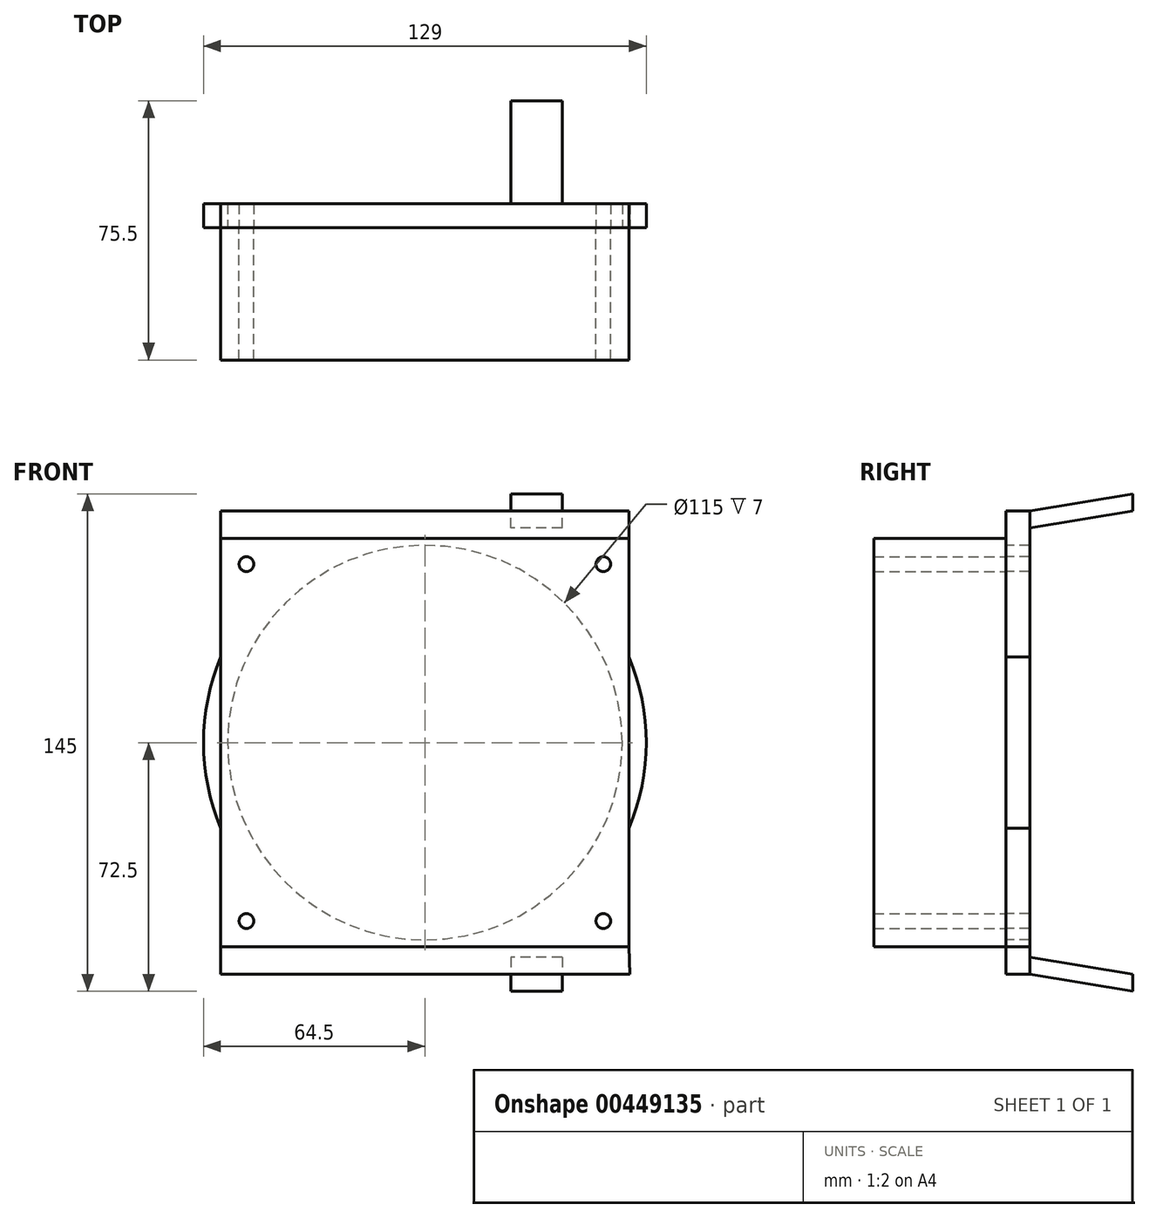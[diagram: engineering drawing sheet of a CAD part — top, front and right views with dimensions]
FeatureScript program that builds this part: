
annotation { "Feature Type Name" : "Feature", "Feature Type Description" : "" }
export const myFeature = defineFeature(function(context is Context, id is Id, definition is map)
    precondition{}
    {
        {
            var Q0;
            Q0=qCreatedBy(makeId("Front.planeOp"),FACE);
            var sketch = newSketch(context, id + "F0", { "sketchPlane" : qUnion([Q0])});
            skLineSegment(sketch, "E0.bottom", {"start": v(-48.5, 67.5) * mm, "end": v(48.5, 67.5) * mm});
            skLineSegment(sketch, "E0.top", {"start": v(-48.5, -67.5) * mm, "end": v(48.5, -67.5) * mm});
            skLineSegment(sketch, "E0.left", {"start": v(-48.5, 67.5) * mm, "end": v(-48.5, -67.5) * mm});
            skLineSegment(sketch, "E0.right", {"start": v(48.5, 67.5) * mm, "end": v(48.5, -67.5) * mm});
            skPoint(sketch, "E0.middle", {"position": v(0, 0) * mm});
            skSolve(sketch);
        }
        {
            var Q0;
            Q0=qCreatedBy(makeId("Front.planeOp"),FACE);
            var sketch = newSketch(context, id + "F1", { "sketchPlane" : qUnion([Q0])});
            skLineSegment(sketch, "E1.bottom", {"start": v(52, 52) * mm, "end": v(-52, 52) * mm, "construction": true});
            skLineSegment(sketch, "E1.top", {"start": v(52, -52) * mm, "end": v(-52, -52) * mm, "construction": true});
            skLineSegment(sketch, "E1.left", {"start": v(52, 52) * mm, "end": v(52, -52) * mm, "construction": true});
            skLineSegment(sketch, "E1.right", {"start": v(-52, 52) * mm, "end": v(-52, -52) * mm, "construction": true});
            skPoint(sketch, "E1.middle", {"position": v(0, 0) * mm});
            skLineSegment(sketch, "E2.bottom", {"start": v(-59.5, -59.5) * mm, "end": v(59.5, -59.5) * mm});
            skLineSegment(sketch, "E2.top", {"start": v(-59.5, 59.5) * mm, "end": v(59.5, 59.5) * mm});
            skLineSegment(sketch, "E2.left", {"start": v(-59.5, -59.5) * mm, "end": v(-59.5, 59.5) * mm});
            skLineSegment(sketch, "E2.right", {"start": v(59.5, -59.5) * mm, "end": v(59.5, 59.5) * mm});
            skCircle(sketch, "E3", {"center": v(-52, 52) * mm, "radius": 2.15 * mm});
            skCircle(sketch, "E4.MirrorC", {"center": v(52, 52) * mm, "radius": 2.15 * mm});
            skCircle(sketch, "E5.MirrorC", {"center": v(-52, -52) * mm, "radius": 2.15 * mm});
            skCircle(sketch, "E6.MirrorC", {"center": v(52, -52) * mm, "radius": 2.15 * mm});
            skSolve(sketch);
        }
        {
            var Q0;
            Q0 = qSketchRegion(id + "F1", true);
            extrude(context, id + "F2", {"entities" : qUnion([Q0]), "depth" : 38.5 * mm});
        }
        {
            var Q0;
            Q0=qCreatedBy(makeId("Front.planeOp"),FACE);
            var sketch = newSketch(context, id + "F3", { "sketchPlane" : qUnion([Q0])});
            skCircle(sketch, "E7.0", {"center": v(52, 52) * mm, "radius": 2.15 * mm});
            skCircle(sketch, "E8.0", {"center": v(52, -52) * mm, "radius": 2.15 * mm});
            skCircle(sketch, "E9.0", {"center": v(-52, -52) * mm, "radius": 2.15 * mm});
            skCircle(sketch, "E10.0", {"center": v(-52, 52) * mm, "radius": 2.15 * mm});
            skLineSegment(sketch, "E11.0", {"start": v(59.5, -59.5) * mm, "end": v(59.5, -24.9) * mm});
            skLineSegment(sketch, "E12.0", {"start": v(-59.5, -59.5) * mm, "end": v(-59.5, -24.9) * mm});
            skCircle(sketch, "E13", {"center": v(0, 0) * mm, "radius": 57.5 * mm});
            skLineSegment(sketch, "E14.trimOffspring", {"start": v(-59.5, 24.9) * mm, "end": v(-59.5, 59.5) * mm});
            skArc(sketch, "E15.trimOffspring", {"start": v(-59.5, 24.9) * mm, "mid": v(-64.5, 0) * mm, "end": v(-59.5, -24.9) * mm});
            skArc(sketch, "E16.trimOffspring", {"start": v(59.5, -24.9) * mm, "mid": v(64.5, 0) * mm, "end": v(59.5, 24.9) * mm});
            skLineSegment(sketch, "E17.trimOffspring", {"start": v(59.5, 24.9) * mm, "end": v(59.5, 59.5) * mm});
            skPoint(sketch, "E18.0", {"position": v(48.5, 67.5) * mm});
            skPoint(sketch, "E19.0", {"position": v(-48.5, 67.5) * mm});
            skPoint(sketch, "E20.0", {"position": v(-48.5, -67.5) * mm});
            skPoint(sketch, "E21.0", {"position": v(48.5, -67.5) * mm});
            skLineSegment(sketch, "E22", {"start": v(59.76, -67.5) * mm, "end": v(-59.5, -67.5) * mm});
            skLineSegment(sketch, "E23", {"start": v(59.5, 67.5) * mm, "end": v(-59.5, 67.5) * mm});
            skLineSegment(sketch, "E24", {"start": v(59.5, 59.5) * mm, "end": v(59.5, 67.5) * mm});
            skLineSegment(sketch, "E25", {"start": v(-59.5, 59.5) * mm, "end": v(-59.5, 67.5) * mm});
            skLineSegment(sketch, "E26", {"start": v(59.5, -59.5) * mm, "end": v(59.76, -67.5) * mm});
            skLineSegment(sketch, "E27", {"start": v(-59.5, -59.5) * mm, "end": v(-59.5, -67.5) * mm});
            skSolve(sketch);
        }
        {
            var Q0;
            Q0 = qSketchRegion(id + "F3", true);
            extrude(context, id + "F4", {"entities" : qUnion([Q0]), "oppositeDirection" : true, "depth" : 7 * mm});
        }
        {
            var Q0;
            Q0=qCreatedBy(makeId("Right.planeOp"),FACE);
            var sketch = newSketch(context, id + "F5", { "sketchPlane" : qUnion([Q0])});
            skPoint(sketch, "E28.0", {"position": v(7, 67.5) * mm});
            skPoint(sketch, "E29.0", {"position": v(7, -67.5) * mm});
            skLineSegment(sketch, "E30", {"start": v(7, 67.5) * mm, "end": v(37, 72.5) * mm});
            skLineSegment(sketch, "E31", {"start": v(37, 72.5) * mm, "end": v(37, 67.5) * mm});
            skLineSegment(sketch, "E32", {"start": v(37, 67.5) * mm, "end": v(7, 62.5) * mm});
            skLineSegment(sketch, "E33", {"start": v(7, 62.5) * mm, "end": v(7, 67.5) * mm});
            skLineSegment(sketch, "E34.MirrorCS", {"start": v(7, -62.5) * mm, "end": v(7, -67.5) * mm});
            skLineSegment(sketch, "E35.MirrorCS", {"start": v(37, -72.5) * mm, "end": v(37, -67.5) * mm});
            skLineSegment(sketch, "E36.MirrorCS", {"start": v(7, -67.5) * mm, "end": v(37, -72.5) * mm});
            skLineSegment(sketch, "E37.MirrorCS", {"start": v(37, -67.5) * mm, "end": v(7, -62.5) * mm});
            skSolve(sketch);
        }
        {
            var Q0;
            Q0 = qSketchRegion(id + "F5", true);
            extrude(context, id + "F6", {"entities" : qUnion([Q0]), "operationType" : NewBodyOperationType.ADD, "depth" : 40 * mm, "hasSecondDirection" : true, "secondDirectionOppositeDirection" : false, "secondDirectionDepth" : (40 - 15) * mm});
        }
    });
